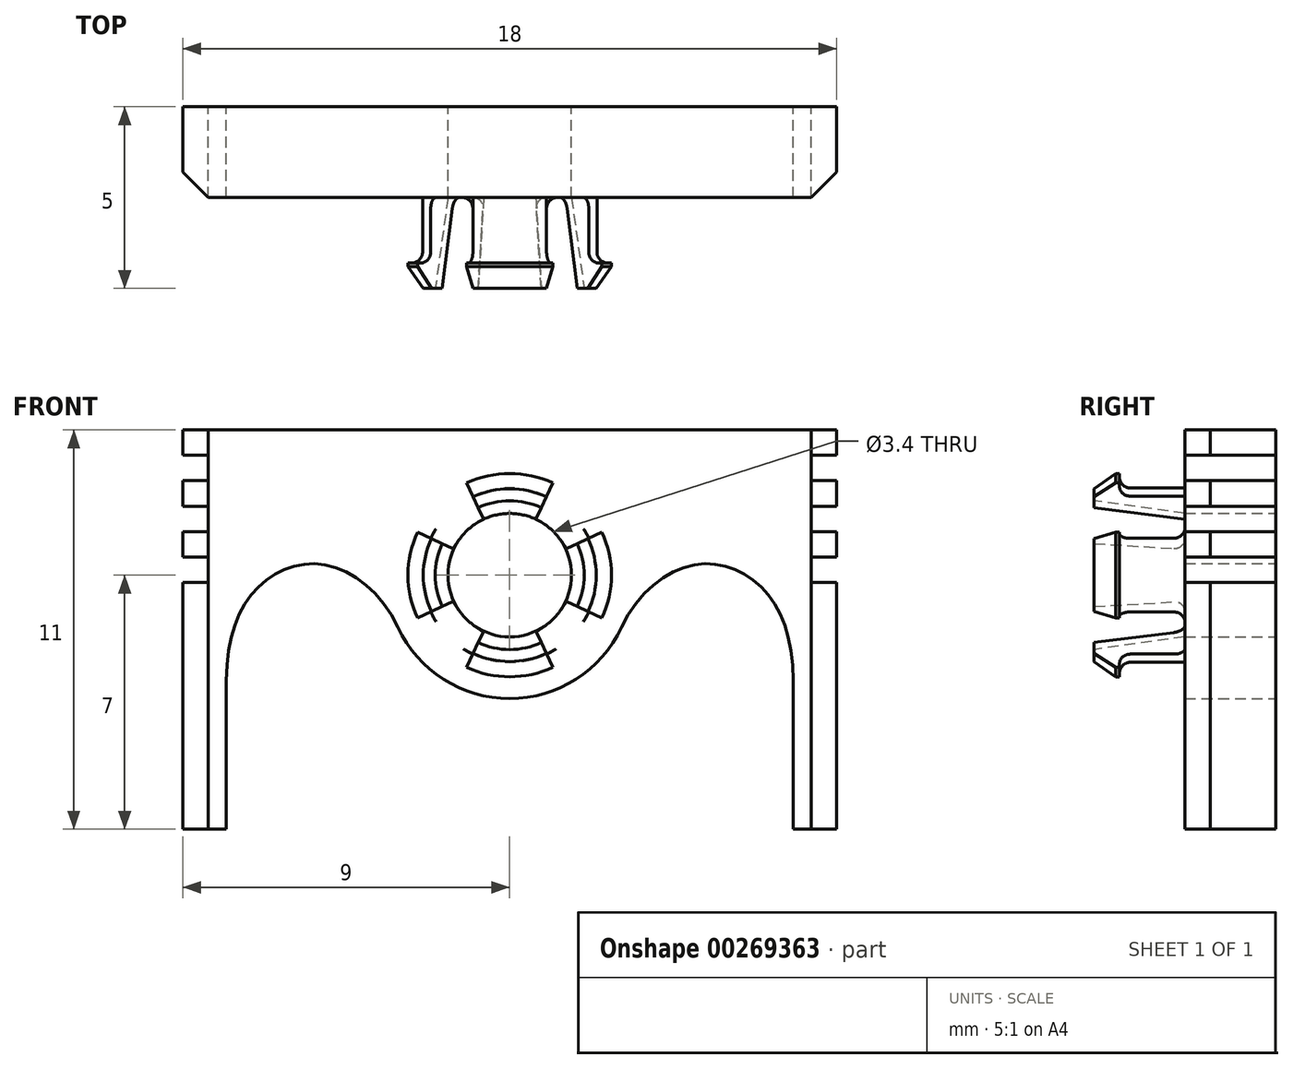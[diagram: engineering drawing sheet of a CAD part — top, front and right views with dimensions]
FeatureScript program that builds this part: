
annotation { "Feature Type Name" : "Feature", "Feature Type Description" : "" }
export const myFeature = defineFeature(function(context is Context, id is Id, definition is map)
    precondition{}
    {
        {
            var Q0;
            Q0=qCreatedBy(makeId("Front.planeOp"),FACE);
            var sketch = newSketch(context, id + "F0", { "sketchPlane" : qUnion([Q0])});
            skLineSegment(sketch, "E0", {"start": v(0, -3.4) * mm, "end": v(0, 25.06) * mm, "construction": true});
            skLineSegment(sketch, "E1.bottom", {"start": v(-9, 4) * mm, "end": v(0, 4) * mm});
            skLineSegment(sketch, "E1.left", {"start": v(-9, 4) * mm, "end": v(-9, 3.3) * mm});
            skArc(sketch, "E2", {"start": v(0, 2.4) * mm, "mid": v(-2.4, 0) * mm, "end": v(0, -2.4) * mm});
            skLineSegment(sketch, "E3.bottom", {"start": v(-9, 3.3) * mm, "end": v(-8.3, 3.3) * mm});
            skLineSegment(sketch, "E3.top", {"start": v(-9, 2.6) * mm, "end": v(-8.3, 2.6) * mm});
            skLineSegment(sketch, "E3.right", {"start": v(-8.3, 3.3) * mm, "end": v(-8.3, 2.6) * mm});
            skLineSegment(sketch, "E4.bottom", {"start": v(-9, 1.9) * mm, "end": v(-8.3, 1.9) * mm});
            skLineSegment(sketch, "E4.top", {"start": v(-9, 1.2) * mm, "end": v(-8.3, 1.2) * mm});
            skLineSegment(sketch, "E4.right", {"start": v(-8.3, 1.9) * mm, "end": v(-8.3, 1.2) * mm});
            skLineSegment(sketch, "E5", {"start": v(-9, 1.9) * mm, "end": v(-9, 2.6) * mm});
            skLineSegment(sketch, "E6", {"start": v(-9, -7) * mm, "end": v(-9, -0.2) * mm});
            skLineSegment(sketch, "E7", {"start": v(-9, -7) * mm, "end": v(-7.8, -7) * mm});
            skLineSegment(sketch, "E8", {"start": v(-7.8, -7) * mm, "end": v(-7.8, -2.9) * mm});
            skLineSegment(sketch, "E9", {"start": v(0, 4) * mm, "end": v(0, 2.4) * mm});
            skLineSegment(sketch, "E10", {"start": v(0, -2.4) * mm, "end": v(0, -3.4) * mm});
            skArc(sketch, "E11", {"start": v(-3.08, -1.44) * mm, "mid": v(-1.83, -2.87) * mm, "end": v(0, -3.4) * mm});
            skFitSpline(sketch, "E12", {"points": [v(-7.8, -2.9) * mm, v(-6.88, -0.29) * mm, v(-5.1, 0.29) * mm, v(-3.08, -1.44) * mm], "startDerivative": vector(0, 10.2) * mm, "endDerivative": vector(3.83, -8.2) * mm});
            skLineSegment(sketch, "E13", {"start": v(-3.08, -1.44) * mm, "end": v(-4.16, 0.88) * mm, "construction": true});
            skLineSegment(sketch, "E14", {"start": v(-9, 0.5) * mm, "end": v(-8.3, 0.5) * mm});
            skLineSegment(sketch, "E15", {"start": v(-8.3, 0.5) * mm, "end": v(-8.3, -0.2) * mm});
            skLineSegment(sketch, "E16", {"start": v(-8.3, -0.2) * mm, "end": v(-9, -0.2) * mm});
            skLineSegment(sketch, "E17.trimOffspring", {"start": v(-9, 0.5) * mm, "end": v(-9, 1.2) * mm});
            skSolve(sketch);
        }
        {
            var Q0;
            Q0=makeQuery(id+"F0.imprint","IMPRINT",FACE,{"disambiguationData":[TD([[makeQuery(id+"F0.imprint","IMPRINT",EDGE,{"derivedFrom":sQuery(id+"F0.wireOp",EDGE,"E1.bottom")}),-1.0]])]});
            extrude(context, id + "F1", {"entities" : qUnion([Q0]), "depth" : 2.5 * mm});
        }
        {
            var Q0;
            Q0=makeQuery(id+"F1.opExtrude","SWEPT_BODY",BODY,{"disambiguationData":[OSD([sQuery(id+"F0.wireOp",EDGE,"E1.bottom"),sQuery(id+"F0.wireOp",EDGE,"E1.left"),sQuery(id+"F0.wireOp",EDGE,"E2"),sQuery(id+"F0.wireOp",EDGE,"E3.bottom"),sQuery(id+"F0.wireOp",EDGE,"E3.top"),sQuery(id+"F0.wireOp",EDGE,"E3.right"),sQuery(id+"F0.wireOp",EDGE,"E4.bottom"),sQuery(id+"F0.wireOp",EDGE,"E4.top"),sQuery(id+"F0.wireOp",EDGE,"E4.right"),sQuery(id+"F0.wireOp",EDGE,"E5"),sQuery(id+"F0.wireOp",EDGE,"E6"),sQuery(id+"F0.wireOp",EDGE,"E7"),sQuery(id+"F0.wireOp",EDGE,"E8"),sQuery(id+"F0.wireOp",EDGE,"E9"),sQuery(id+"F0.wireOp",EDGE,"E10"),sQuery(id+"F0.wireOp",EDGE,"E11"),sQuery(id+"F0.wireOp",EDGE,"E12"),sQuery(id+"F0.wireOp",EDGE,"E14"),sQuery(id+"F0.wireOp",EDGE,"E15"),sQuery(id+"F0.wireOp",EDGE,"E16"),sQuery(id+"F0.wireOp",EDGE,"E17.trimOffspring")])]});
            var Q1;
            Q1=qCreatedBy(makeId("Right.planeOp"),FACE);
            mirror(context, id + "F2", {"operationType" : NewBodyOperationType.ADD, "entities" : qUnion([Q0]), "mirrorPlane" : qUnion([Q1])});
        }
        {
            var Q0;
            Q0=qCreatedBy(makeId("Right.planeOp"),FACE);
            var sketch = newSketch(context, id + "F3", { "sketchPlane" : qUnion([Q0])});
            skLineSegment(sketch, "E18", {"start": v(0, 0) * mm, "end": v(-7.95, 0) * mm, "construction": true});
            skLineSegment(sketch, "E19", {"start": v(0, 0) * mm, "end": v(0, 4.28) * mm, "construction": true});
            skLineSegment(sketch, "E20", {"start": v(2.05, 2.4) * mm, "end": v(-4.2, 2.4) * mm, "construction": true});
            skLineSegment(sketch, "E21", {"start": v(-2.5, -2.14) * mm, "end": v(-2.5, 4.96) * mm, "construction": true});
            skLineSegment(sketch, "E22", {"start": v(0, 2.4) * mm, "end": v(0, 1.7) * mm});
            skLineSegment(sketch, "E23", {"start": v(0, 1.7) * mm, "end": v(-5, 1.7) * mm});
            skLineSegment(sketch, "E24", {"start": v(-5, 1.7) * mm, "end": v(-5, 2.8) * mm});
            skLineSegment(sketch, "E25", {"start": v(-5, 2.8) * mm, "end": v(-4.3, 2.8) * mm});
            skLineSegment(sketch, "E26", {"start": v(-4.3, 2.8) * mm, "end": v(-4.3, 2.4) * mm});
            skLineSegment(sketch, "E27", {"start": v(-4.3, 2.4) * mm, "end": v(0, 2.4) * mm});
            skSolve(sketch);
        }
        {
            var Q0;
            Q0=makeQuery(id+"F3.imprint","IMPRINT",FACE,{"disambiguationData":[TD([[makeQuery(id+"F3.imprint","IMPRINT",EDGE,{"derivedFrom":sQuery(id+"F3.wireOp",EDGE,"E22")}),-1.0]])]});
            var Q1;
            Q1=sQuery(id+"F3.wireOp",EDGE,"E18");
            revolve(context, id + "F4", {"operationType" : NewBodyOperationType.ADD, "entities" : qUnion([Q0]), "axis" : qUnion([Q1]), "revolveType" : RevolveType.FULL});
        }
        {
            var Q0;
            Q0=makeQuery(id+"F4.opRevolve","SWEPT_EDGE",EDGE,{"disambiguationData":[OSD([sQuery(id+"F3.wireOp",EDGE,"E23"),sQuery(id+"F3.wireOp",EDGE,"E24")])]});
            chamfer(context, id + "F5", {"entities" : qUnion([Q0]), "chamferType" : ChamferType.TWO_OFFSETS, "width1" : 0.35 * mm, "oppositeDirection" : false, "width2" : 2.5 * mm, "tangentPropagation" : true});
        }
        {
            var Q0;
            Q0=makeQuery(id+"F4.opRevolve","SWEPT_FACE",FACE,{"disambiguationData":[OSD([sQuery(id+"F3.wireOp",EDGE,"E24")])]});
            var sketch = newSketch(context, id + "F6", { "sketchPlane" : qUnion([Q0])});
            skLineSegment(sketch, "E28", {"start": v(-4.34, 4.34) * mm, "end": v(4.98, -4.98) * mm, "construction": true});
            skLineSegment(sketch, "E29", {"start": v(-3.35, -3.35) * mm, "end": v(2.96, 2.96) * mm, "construction": true});
            skCircle(sketch, "E30", {"center": v(0, 0) * mm, "radius": 3.5 * mm});
            skLineSegment(sketch, "E31", {"start": v(1.48, -3.17) * mm, "end": v(-1.48, 3.17) * mm});
            skLineSegment(sketch, "E32", {"start": v(3.17, -1.48) * mm, "end": v(-3.17, 1.48) * mm});
            skLineSegment(sketch, "E33", {"start": v(0, -10.04) * mm, "end": v(0, 8.69) * mm, "construction": true});
            skLineSegment(sketch, "E34", {"start": v(3.17, 1.48) * mm, "end": v(-3.17, -1.48) * mm});
            skLineSegment(sketch, "E35", {"start": v(-1.48, -3.17) * mm, "end": v(1.48, 3.17) * mm});
            skSolve(sketch);
        }
        {
            var Q0;
            Q0=makeQuery(id+"F4.opRevolve","SWEPT_EDGE",EDGE,{"disambiguationData":[OSD([sQuery(id+"F3.wireOp",EDGE,"E24"),sQuery(id+"F3.wireOp",EDGE,"E25")])]});
            chamfer(context, id + "F7", {"entities" : qUnion([Q0]), "chamferType" : ChamferType.OFFSET_ANGLE, "width" : 0.6 * mm, "oppositeDirection" : false, "angle" : 35 * degree, "tangentPropagation" : true});
        }
        {
            var Q0;
            Q0=makeQuery(id+"F4.opRevolve","SWEPT_EDGE",EDGE,{"disambiguationData":[OSD([sQuery(id+"F3.wireOp",EDGE,"E26"),sQuery(id+"F3.wireOp",EDGE,"E27")])]});
            fillet(context, id + "F8", {"entities" : qUnion([Q0]), "radius" : 0.3 * mm, "tangentPropagation" : true, "allowEdgeOverflow" : false});
        }
        {
            var Q0;
            {var subQ0=sQuery(id+"F6.wireOp",EDGE,"E32");var subQ1=sQuery(id+"F6.wireOp",EDGE,"E31");var subQ2=makeQuery(id+"F6.imprint","INTERSECT",VERTEX,{"derivedFrom":[subQ1,subQ0,sQuery(id+"F6.wireOp",EDGE,"E34"),sQuery(id+"F6.wireOp",EDGE,"E35")]});Q0=makeQuery(id+"F6.imprint","IMPRINT",FACE,{"disambiguationData":[TD([[makeQuery(id+"F6.imprint","IMPRINT",EDGE,{"disambiguationData":[TD([[subQ2,-1.0]])],"derivedFrom":subQ1}),1.0]])]});}
            var Q1;
            {var subQ0=sQuery(id+"F6.wireOp",EDGE,"E31");var subQ1=sQuery(id+"F3.wireOp",EDGE,"E24");var subQ4=makeQuery(id+"F4.opRevolve","SWEPT_EDGE",EDGE,{"disambiguationData":[OSD([subQ1,sQuery(id+"F3.wireOp",EDGE,"E25")])]});var subQ5=makeQuery(id+"F6.imprint","INTERSECT",VERTEX,{"disambiguationData":[OD(1.0)],"derivedFrom":[subQ4,subQ0]});Q1=makeQuery(id+"F6.imprint","IMPRINT",FACE,{"disambiguationData":[TD([[makeQuery(id+"F6.imprint","IMPRINT",EDGE,{"disambiguationData":[TD([[subQ5,1.0]])],"derivedFrom":subQ0}),1.0]])]});}
            var Q2;
            {var subQ0=sQuery(id+"F6.wireOp",EDGE,"E31");var subQ1=sQuery(id+"F6.wireOp",EDGE,"E30");var subQ2=makeQuery(id+"F6.imprint","INTERSECT",VERTEX,{"disambiguationData":[OD(1.0)],"derivedFrom":[subQ1,subQ0]});Q2=makeQuery(id+"F6.imprint","IMPRINT",FACE,{"disambiguationData":[TD([[makeQuery(id+"F6.imprint","IMPRINT",EDGE,{"disambiguationData":[TD([[subQ2,-1.0]])],"derivedFrom":subQ1}),1.0]])]});}
            var Q3;
            {var subQ0=sQuery(id+"F6.wireOp",EDGE,"E34");var subQ1=sQuery(id+"F6.wireOp",EDGE,"E30");var subQ2=makeQuery(id+"F6.imprint","INTERSECT",VERTEX,{"disambiguationData":[OD(1.0)],"derivedFrom":[subQ1,subQ0]});Q3=makeQuery(id+"F6.imprint","IMPRINT",FACE,{"disambiguationData":[TD([[makeQuery(id+"F6.imprint","IMPRINT",EDGE,{"disambiguationData":[TD([[subQ2,-1.0]])],"derivedFrom":subQ1}),1.0]])]});}
            var Q4;
            {var subQ0=sQuery(id+"F6.wireOp",EDGE,"E35");var subQ1=sQuery(id+"F6.wireOp",EDGE,"E34");var subQ2=makeQuery(id+"F6.imprint","INTERSECT",VERTEX,{"derivedFrom":[sQuery(id+"F6.wireOp",EDGE,"E31"),sQuery(id+"F6.wireOp",EDGE,"E32"),subQ1,subQ0]});Q4=makeQuery(id+"F6.imprint","IMPRINT",FACE,{"disambiguationData":[TD([[makeQuery(id+"F6.imprint","IMPRINT",EDGE,{"disambiguationData":[TD([[subQ2,-1.0]])],"derivedFrom":subQ1}),1.0]])]});}
            var Q5;
            {var subQ0=sQuery(id+"F6.wireOp",EDGE,"E34");var subQ1=sQuery(id+"F3.wireOp",EDGE,"E24");var subQ4=makeQuery(id+"F4.opRevolve","SWEPT_EDGE",EDGE,{"disambiguationData":[OSD([subQ1,sQuery(id+"F3.wireOp",EDGE,"E25")])]});var subQ5=makeQuery(id+"F6.imprint","INTERSECT",VERTEX,{"disambiguationData":[OD(1.0)],"derivedFrom":[subQ4,subQ0]});Q5=makeQuery(id+"F6.imprint","IMPRINT",FACE,{"disambiguationData":[TD([[makeQuery(id+"F6.imprint","IMPRINT",EDGE,{"disambiguationData":[TD([[subQ5,1.0]])],"derivedFrom":subQ0}),1.0]])]});}
            var Q6;
            {var subQ0=sQuery(id+"F6.wireOp",EDGE,"E31");var subQ1=sQuery(id+"F6.wireOp",EDGE,"E30");var subQ2=makeQuery(id+"F6.imprint","INTERSECT",VERTEX,{"disambiguationData":[OD(0.0)],"derivedFrom":[subQ1,subQ0]});Q6=makeQuery(id+"F6.imprint","IMPRINT",FACE,{"disambiguationData":[TD([[makeQuery(id+"F6.imprint","IMPRINT",EDGE,{"disambiguationData":[TD([[subQ2,-1.0]])],"derivedFrom":subQ1}),1.0]])]});}
            var Q7;
            {var subQ0=sQuery(id+"F6.wireOp",EDGE,"E31");var subQ1=sQuery(id+"F3.wireOp",EDGE,"E24");var subQ2=makeQuery(id+"F4.opRevolve","SWEPT_EDGE",EDGE,{"disambiguationData":[OSD([subQ1,sQuery(id+"F3.wireOp",EDGE,"E25")])]});var subQ3=makeQuery(id+"F6.imprint","INTERSECT",VERTEX,{"disambiguationData":[OD(0.0)],"derivedFrom":[subQ2,subQ0]});Q7=makeQuery(id+"F6.imprint","IMPRINT",FACE,{"disambiguationData":[TD([[makeQuery(id+"F6.imprint","IMPRINT",EDGE,{"disambiguationData":[TD([[subQ3,-1.0]])],"derivedFrom":subQ0}),-1.0]])]});}
            var Q8;
            {var subQ0=sQuery(id+"F6.wireOp",EDGE,"E32");var subQ1=sQuery(id+"F6.wireOp",EDGE,"E31");var subQ2=makeQuery(id+"F6.imprint","INTERSECT",VERTEX,{"derivedFrom":[subQ1,subQ0,sQuery(id+"F6.wireOp",EDGE,"E34"),sQuery(id+"F6.wireOp",EDGE,"E35")]});Q8=makeQuery(id+"F6.imprint","IMPRINT",FACE,{"disambiguationData":[TD([[makeQuery(id+"F6.imprint","IMPRINT",EDGE,{"disambiguationData":[TD([[subQ2,1.0]])],"derivedFrom":subQ1}),-1.0]])]});}
            var Q9;
            {var subQ0=sQuery(id+"F6.wireOp",EDGE,"E35");var subQ1=sQuery(id+"F6.wireOp",EDGE,"E34");var subQ2=makeQuery(id+"F6.imprint","INTERSECT",VERTEX,{"derivedFrom":[sQuery(id+"F6.wireOp",EDGE,"E31"),sQuery(id+"F6.wireOp",EDGE,"E32"),subQ1,subQ0]});Q9=makeQuery(id+"F6.imprint","IMPRINT",FACE,{"disambiguationData":[TD([[makeQuery(id+"F6.imprint","IMPRINT",EDGE,{"disambiguationData":[TD([[subQ2,1.0]])],"derivedFrom":subQ1}),-1.0]])]});}
            var Q10;
            {var subQ0=sQuery(id+"F6.wireOp",EDGE,"E34");var subQ1=sQuery(id+"F3.wireOp",EDGE,"E24");var subQ2=makeQuery(id+"F4.opRevolve","SWEPT_EDGE",EDGE,{"disambiguationData":[OSD([subQ1,sQuery(id+"F3.wireOp",EDGE,"E25")])]});var subQ3=makeQuery(id+"F6.imprint","INTERSECT",VERTEX,{"disambiguationData":[OD(0.0)],"derivedFrom":[subQ2,subQ0]});Q10=makeQuery(id+"F6.imprint","IMPRINT",FACE,{"disambiguationData":[TD([[makeQuery(id+"F6.imprint","IMPRINT",EDGE,{"disambiguationData":[TD([[subQ3,-1.0]])],"derivedFrom":subQ0}),-1.0]])]});}
            var Q11;
            {var subQ0=sQuery(id+"F6.wireOp",EDGE,"E34");var subQ1=sQuery(id+"F6.wireOp",EDGE,"E30");var subQ2=makeQuery(id+"F6.imprint","INTERSECT",VERTEX,{"disambiguationData":[OD(0.0)],"derivedFrom":[subQ1,subQ0]});Q11=makeQuery(id+"F6.imprint","IMPRINT",FACE,{"disambiguationData":[TD([[makeQuery(id+"F6.imprint","IMPRINT",EDGE,{"disambiguationData":[TD([[subQ2,-1.0]])],"derivedFrom":subQ1}),1.0]])]});}
            extrude(context, id + "F9", {"entities" : qUnion([Q0, Q1, Q2, Q3, Q4, Q5, Q6, Q7, Q8, Q9, Q10, Q11]), "operationType" : NewBodyOperationType.REMOVE, "oppositeDirection" : true, "depth" : 2.5 * mm});
        }
        {
            var Q0;
            {var subQ0=sQuery(id+"F6.wireOp",EDGE,"E31");var subQ1=sQuery(id+"F3.wireOp",EDGE,"E24");Q0=makeQuery(id+"F9.boolean.opBoolean","COPY",EDGE,{"derivedFrom":makeQuery(id+"F9.opExtrude","CAP_EDGE",EDGE,{"disambiguationData":[OSD([subQ0]),TDD([makeQuery(id+"F6.imprint","IMPRINT",EDGE,{"disambiguationData":[TD([[makeQuery(id+"F6.imprint","INTERSECT",VERTEX,{"disambiguationData":[OD(1.0)],"derivedFrom":[makeQuery(id+"F4.opRevolve","SWEPT_EDGE",EDGE,{"disambiguationData":[OSD([sQuery(id+"F3.wireOp",EDGE,"E23"),subQ1])]}),subQ0]}),-1.0]])],"derivedFrom":subQ0}),makeQuery(id+"F6.imprint","IMPRINT",EDGE,{"disambiguationData":[TD([[makeQuery(id+"F6.imprint","INTERSECT",VERTEX,{"disambiguationData":[OD(1.0)],"derivedFrom":[sQuery(id+"F6.wireOp",EDGE,"E30"),subQ0]}),1.0]])],"derivedFrom":subQ0})])],"isStart":false})});}
            var Q1;
            {var subQ0=sQuery(id+"F6.wireOp",EDGE,"E32");var subQ1=sQuery(id+"F3.wireOp",EDGE,"E24");Q1=makeQuery(id+"F9.boolean.opBoolean","COPY",EDGE,{"derivedFrom":makeQuery(id+"F9.opExtrude","CAP_EDGE",EDGE,{"disambiguationData":[OSD([subQ0]),TDD([makeQuery(id+"F6.imprint","IMPRINT",EDGE,{"disambiguationData":[TD([[makeQuery(id+"F6.imprint","INTERSECT",VERTEX,{"disambiguationData":[OD(1.0)],"derivedFrom":[makeQuery(id+"F4.opRevolve","SWEPT_EDGE",EDGE,{"disambiguationData":[OSD([sQuery(id+"F3.wireOp",EDGE,"E23"),subQ1])]}),subQ0]}),-1.0]])],"derivedFrom":subQ0}),makeQuery(id+"F6.imprint","IMPRINT",EDGE,{"disambiguationData":[TD([[makeQuery(id+"F6.imprint","INTERSECT",VERTEX,{"disambiguationData":[OD(1.0)],"derivedFrom":[sQuery(id+"F6.wireOp",EDGE,"E30"),subQ0]}),1.0]])],"derivedFrom":subQ0})])],"isStart":false})});}
            var Q2;
            {var subQ0=sQuery(id+"F6.wireOp",EDGE,"E34");var subQ1=sQuery(id+"F3.wireOp",EDGE,"E24");Q2=makeQuery(id+"F9.boolean.opBoolean","COPY",EDGE,{"derivedFrom":makeQuery(id+"F9.opExtrude","CAP_EDGE",EDGE,{"disambiguationData":[OSD([subQ0]),TDD([makeQuery(id+"F6.imprint","IMPRINT",EDGE,{"disambiguationData":[TD([[makeQuery(id+"F6.imprint","INTERSECT",VERTEX,{"disambiguationData":[OD(1.0)],"derivedFrom":[makeQuery(id+"F4.opRevolve","SWEPT_EDGE",EDGE,{"disambiguationData":[OSD([sQuery(id+"F3.wireOp",EDGE,"E23"),subQ1])]}),subQ0]}),-1.0]])],"derivedFrom":subQ0}),makeQuery(id+"F6.imprint","IMPRINT",EDGE,{"disambiguationData":[TD([[makeQuery(id+"F6.imprint","INTERSECT",VERTEX,{"disambiguationData":[OD(1.0)],"derivedFrom":[sQuery(id+"F6.wireOp",EDGE,"E30"),subQ0]}),1.0]])],"derivedFrom":subQ0})])],"isStart":false})});}
            var Q3;
            {var subQ0=sQuery(id+"F6.wireOp",EDGE,"E35");var subQ1=sQuery(id+"F3.wireOp",EDGE,"E24");var subQ2=makeQuery(id+"F6.imprint","INTERSECT",VERTEX,{"disambiguationData":[OD(0.0)],"derivedFrom":[makeQuery(id+"F4.opRevolve","SWEPT_EDGE",EDGE,{"disambiguationData":[OSD([subQ1,sQuery(id+"F3.wireOp",EDGE,"E25")])]}),subQ0]});Q3=makeQuery(id+"F9.boolean.opBoolean","COPY",EDGE,{"derivedFrom":makeQuery(id+"F9.opExtrude","CAP_EDGE",EDGE,{"disambiguationData":[OSD([subQ0]),TDD([makeQuery(id+"F6.imprint","IMPRINT",EDGE,{"disambiguationData":[TD([[makeQuery(id+"F6.imprint","INTERSECT",VERTEX,{"disambiguationData":[OD(0.0)],"derivedFrom":[sQuery(id+"F6.wireOp",EDGE,"E30"),subQ0]}),-1.0]])],"derivedFrom":subQ0}),makeQuery(id+"F6.imprint","IMPRINT",EDGE,{"disambiguationData":[TD([[subQ2,-1.0]])],"derivedFrom":subQ0})])],"isStart":false})});}
            var Q4;
            {var subQ0=sQuery(id+"F6.wireOp",EDGE,"E31");var subQ1=sQuery(id+"F3.wireOp",EDGE,"E24");var subQ2=makeQuery(id+"F6.imprint","INTERSECT",VERTEX,{"disambiguationData":[OD(0.0)],"derivedFrom":[makeQuery(id+"F4.opRevolve","SWEPT_EDGE",EDGE,{"disambiguationData":[OSD([subQ1,sQuery(id+"F3.wireOp",EDGE,"E25")])]}),subQ0]});Q4=makeQuery(id+"F9.boolean.opBoolean","COPY",EDGE,{"derivedFrom":makeQuery(id+"F9.opExtrude","CAP_EDGE",EDGE,{"disambiguationData":[OSD([subQ0]),TDD([makeQuery(id+"F6.imprint","IMPRINT",EDGE,{"disambiguationData":[TD([[makeQuery(id+"F6.imprint","INTERSECT",VERTEX,{"disambiguationData":[OD(0.0)],"derivedFrom":[sQuery(id+"F6.wireOp",EDGE,"E30"),subQ0]}),-1.0]])],"derivedFrom":subQ0}),makeQuery(id+"F6.imprint","IMPRINT",EDGE,{"disambiguationData":[TD([[subQ2,-1.0]])],"derivedFrom":subQ0})])],"isStart":false})});}
            var Q5;
            {var subQ0=sQuery(id+"F6.wireOp",EDGE,"E32");var subQ1=sQuery(id+"F3.wireOp",EDGE,"E24");var subQ2=makeQuery(id+"F6.imprint","INTERSECT",VERTEX,{"disambiguationData":[OD(0.0)],"derivedFrom":[makeQuery(id+"F4.opRevolve","SWEPT_EDGE",EDGE,{"disambiguationData":[OSD([subQ1,sQuery(id+"F3.wireOp",EDGE,"E25")])]}),subQ0]});Q5=makeQuery(id+"F9.boolean.opBoolean","COPY",EDGE,{"derivedFrom":makeQuery(id+"F9.opExtrude","CAP_EDGE",EDGE,{"disambiguationData":[OSD([subQ0]),TDD([makeQuery(id+"F6.imprint","IMPRINT",EDGE,{"disambiguationData":[TD([[makeQuery(id+"F6.imprint","INTERSECT",VERTEX,{"disambiguationData":[OD(0.0)],"derivedFrom":[sQuery(id+"F6.wireOp",EDGE,"E30"),subQ0]}),-1.0]])],"derivedFrom":subQ0}),makeQuery(id+"F6.imprint","IMPRINT",EDGE,{"disambiguationData":[TD([[subQ2,-1.0]])],"derivedFrom":subQ0})])],"isStart":false})});}
            var Q6;
            {var subQ0=sQuery(id+"F6.wireOp",EDGE,"E35");var subQ1=sQuery(id+"F3.wireOp",EDGE,"E24");Q6=makeQuery(id+"F9.boolean.opBoolean","COPY",EDGE,{"derivedFrom":makeQuery(id+"F9.opExtrude","CAP_EDGE",EDGE,{"disambiguationData":[OSD([subQ0]),TDD([makeQuery(id+"F6.imprint","IMPRINT",EDGE,{"disambiguationData":[TD([[makeQuery(id+"F6.imprint","INTERSECT",VERTEX,{"disambiguationData":[OD(1.0)],"derivedFrom":[makeQuery(id+"F4.opRevolve","SWEPT_EDGE",EDGE,{"disambiguationData":[OSD([sQuery(id+"F3.wireOp",EDGE,"E23"),subQ1])]}),subQ0]}),-1.0]])],"derivedFrom":subQ0}),makeQuery(id+"F6.imprint","IMPRINT",EDGE,{"disambiguationData":[TD([[makeQuery(id+"F6.imprint","INTERSECT",VERTEX,{"disambiguationData":[OD(1.0)],"derivedFrom":[sQuery(id+"F6.wireOp",EDGE,"E30"),subQ0]}),1.0]])],"derivedFrom":subQ0})])],"isStart":false})});}
            var Q7;
            {var subQ0=sQuery(id+"F6.wireOp",EDGE,"E34");var subQ1=sQuery(id+"F3.wireOp",EDGE,"E24");var subQ2=makeQuery(id+"F6.imprint","INTERSECT",VERTEX,{"disambiguationData":[OD(0.0)],"derivedFrom":[makeQuery(id+"F4.opRevolve","SWEPT_EDGE",EDGE,{"disambiguationData":[OSD([subQ1,sQuery(id+"F3.wireOp",EDGE,"E25")])]}),subQ0]});Q7=makeQuery(id+"F9.boolean.opBoolean","COPY",EDGE,{"derivedFrom":makeQuery(id+"F9.opExtrude","CAP_EDGE",EDGE,{"disambiguationData":[OSD([subQ0]),TDD([makeQuery(id+"F6.imprint","IMPRINT",EDGE,{"disambiguationData":[TD([[makeQuery(id+"F6.imprint","INTERSECT",VERTEX,{"disambiguationData":[OD(0.0)],"derivedFrom":[sQuery(id+"F6.wireOp",EDGE,"E30"),subQ0]}),-1.0]])],"derivedFrom":subQ0}),makeQuery(id+"F6.imprint","IMPRINT",EDGE,{"disambiguationData":[TD([[subQ2,-1.0]])],"derivedFrom":subQ0})])],"isStart":false})});}
            fillet(context, id + "F10", {"entities" : qUnion([Q0, Q1, Q2, Q3, Q4, Q5, Q6, Q7]), "radius" : 0.3 * mm, "tangentPropagation" : true, "allowEdgeOverflow" : false});
        }
        {
            var Q0;
            Q0=makeQuery(id+"F1.opExtrude","CAP_EDGE",EDGE,{"disambiguationData":[OSD([sQuery(id+"F0.wireOp",EDGE,"E6")])],"isStart":false});
            var Q1;
            Q1=makeQuery(id+"F2.opPattern","COPY",EDGE,{"derivedFrom":makeQuery(id+"F1.opExtrude","CAP_EDGE",EDGE,{"disambiguationData":[OSD([sQuery(id+"F0.wireOp",EDGE,"E6")])],"isStart":false}),"instanceName":"1"});
            var Q2;
            Q2=makeQuery(id+"F1.opExtrude","CAP_EDGE",EDGE,{"disambiguationData":[OSD([sQuery(id+"F0.wireOp",EDGE,"E1.left")])],"isStart":false});
            var Q3;
            Q3=makeQuery(id+"F1.opExtrude","CAP_EDGE",EDGE,{"disambiguationData":[OSD([sQuery(id+"F0.wireOp",EDGE,"E5")])],"isStart":false});
            var Q4;
            Q4=makeQuery(id+"F1.opExtrude","CAP_EDGE",EDGE,{"disambiguationData":[OSD([sQuery(id+"F0.wireOp",EDGE,"E17.trimOffspring")])],"isStart":false});
            var Q5;
            Q5=makeQuery(id+"F2.opPattern","COPY",EDGE,{"derivedFrom":makeQuery(id+"F1.opExtrude","CAP_EDGE",EDGE,{"disambiguationData":[OSD([sQuery(id+"F0.wireOp",EDGE,"E1.left")])],"isStart":false}),"instanceName":"1"});
            var Q6;
            Q6=makeQuery(id+"F2.opPattern","COPY",EDGE,{"derivedFrom":makeQuery(id+"F1.opExtrude","CAP_EDGE",EDGE,{"disambiguationData":[OSD([sQuery(id+"F0.wireOp",EDGE,"E5")])],"isStart":false}),"instanceName":"1"});
            var Q7;
            Q7=makeQuery(id+"F2.opPattern","COPY",EDGE,{"derivedFrom":makeQuery(id+"F1.opExtrude","CAP_EDGE",EDGE,{"disambiguationData":[OSD([sQuery(id+"F0.wireOp",EDGE,"E17.trimOffspring")])],"isStart":false}),"instanceName":"1"});
            chamfer(context, id + "F11", {"entities" : qUnion([Q0, Q1, Q2, Q3, Q4, Q5, Q6, Q7]), "width" : 0.7 * mm, "tangentPropagation" : true});
        }
    });
